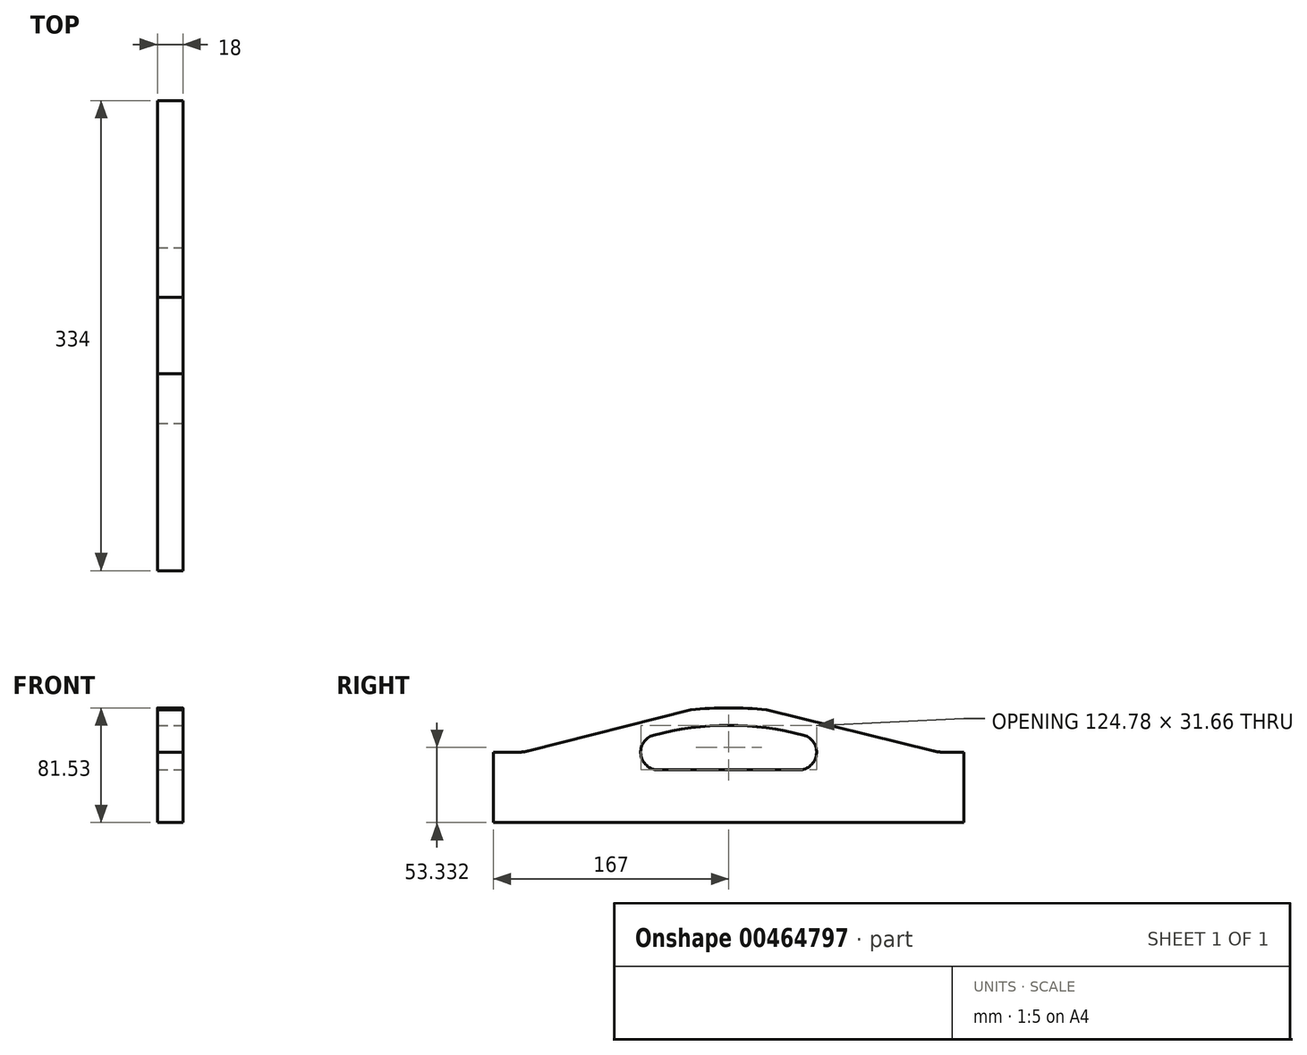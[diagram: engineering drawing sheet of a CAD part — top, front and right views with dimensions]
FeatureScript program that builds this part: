
annotation { "Feature Type Name" : "Feature", "Feature Type Description" : "" }
export const myFeature = defineFeature(function(context is Context, id is Id, definition is map)
    precondition{}
    {
        {
            var Q0;
            Q0=qCreatedBy(makeId("Right.planeOp"),FACE);
            var sketch = newSketch(context, id + "F0", { "sketchPlane" : qUnion([Q0])});
            skLineSegment(sketch, "E0.bottom", {"start": v(0, 0) * mm, "end": v(334, 0) * mm});
            skLineSegment(sketch, "E0.top", {"start": v(0, 100) * mm, "end": v(334, 100) * mm, "construction": true});
            skLineSegment(sketch, "E0.left", {"start": v(0, 0) * mm, "end": v(0, 100) * mm});
            skLineSegment(sketch, "E0.right", {"start": v(334, 0) * mm, "end": v(334, 100) * mm});
            skLineSegment(sketch, "E1", {"start": v(0, 50) * mm, "end": v(17.4, 50) * mm, "construction": true});
            skPoint(sketch, "E2", {"position": v(140, 100) * mm});
            skPoint(sketch, "E3", {"position": v(194, 100) * mm});
            skLineSegment(sketch, "E4", {"start": v(140, 100) * mm, "end": v(140, 0) * mm});
            skLineSegment(sketch, "E5", {"start": v(194, 100) * mm, "end": v(194, 0) * mm});
            skArc(sketch, "E6", {"start": v(140, 80) * mm, "mid": v(167, 81.53) * mm, "end": v(194, 80) * mm});
            skLineSegment(sketch, "E7", {"start": v(0, 50) * mm, "end": v(18, 50) * mm});
            skLineSegment(sketch, "E8", {"start": v(24.73, 50.91) * mm, "end": v(140, 80) * mm});
            skLineSegment(sketch, "E9", {"start": v(334, 50) * mm, "end": v(319.63, 50) * mm});
            skLineSegment(sketch, "E10", {"start": v(312.47, 50.87) * mm, "end": v(194, 80) * mm});
            skPoint(sketch, "E11.newPointB", {"position": v(334, 50) * mm});
            skArc(sketch, "E11.filletArc", {"start": v(17.4, 50) * mm, "mid": v(21.1, 50.23) * mm, "end": v(24.73, 50.91) * mm});
            skPoint(sketch, "E12.visualSharp", {"position": v(316, 50) * mm});
            skArc(sketch, "E12.filletArc", {"start": v(312.47, 50.87) * mm, "mid": v(316.03, 50.22) * mm, "end": v(319.63, 50) * mm});
            skSolve(sketch);
        }
        {
            var Q0;
            Q0=qSketchRegion(id+"F0",true);
            extrude(context, id + "F1", {"entities" : qUnion([Q0]), "depth" : 18 * mm});
        }
        {
            var Q0;
            Q0=makeQuery(id+"F1.opExtrude","CAP_FACE",FACE,{"disambiguationData":[OSD([sQuery(id+"F0.wireOp",EDGE,"E0.bottom"),sQuery(id+"F0.wireOp",EDGE,"E0.left"),sQuery(id+"F0.wireOp",EDGE,"E0.right"),sQuery(id+"F0.wireOp",EDGE,"hojcP1TL-Xpnx-iaRk-RxsB-XFSz29LCahgp"),sQuery(id+"F0.wireOp",EDGE,"atJYV5Rb-Yel0-aSoY-TR2I-Oknle9Pxrf5G"),sQuery(id+"F0.wireOp",EDGE,"E6")])],"isStart":false});
            var sketch = newSketch(context, id + "F2", { "sketchPlane" : qUnion([Q0])});
            skLineSegment(sketch, "E13", {"start": v(117, 62.5) * mm, "end": v(117, 37.5) * mm, "construction": true});
            skLineSegment(sketch, "E14", {"start": v(217, 62.5) * mm, "end": v(217, 37.5) * mm, "construction": true});
            skLineSegment(sketch, "E15", {"start": v(117, 37.5) * mm, "end": v(217, 37.5) * mm});
            skArc(sketch, "E16", {"start": v(104.5, 50) * mm, "mid": v(108.16, 41.16) * mm, "end": v(117, 37.5) * mm});
            skArc(sketch, "E17", {"start": v(217, 37.5) * mm, "mid": v(225.84, 41.16) * mm, "end": v(229.5, 50) * mm});
            skLineSegment(sketch, "E18", {"start": v(167, 50) * mm, "end": v(167, -134.27) * mm, "construction": true});
            skLineSegment(sketch, "E19", {"start": v(167, -134.27) * mm, "end": v(117, 50) * mm, "construction": true});
            skLineSegment(sketch, "E20", {"start": v(167, -134.27) * mm, "end": v(217, 50) * mm, "construction": true});
            skLineSegment(sketch, "E21", {"start": v(117, 50) * mm, "end": v(110.86, 72.65) * mm, "construction": true});
            skLineSegment(sketch, "E22", {"start": v(217, 50) * mm, "end": v(223.2, 72.82) * mm, "construction": true});
            skArc(sketch, "E23", {"start": v(113.73, 62.06) * mm, "mid": v(107.07, 57.6) * mm, "end": v(104.5, 50) * mm});
            skArc(sketch, "E24", {"start": v(229.5, 50) * mm, "mid": v(226.93, 57.6) * mm, "end": v(220.27, 62.06) * mm});
            skArc(sketch, "E25", {"start": v(113.73, 62.06) * mm, "mid": v(167, 69.16) * mm, "end": v(220.27, 62.06) * mm});
            skLineSegment(sketch, "E26", {"start": v(0, 50) * mm, "end": v(334, 50) * mm, "construction": true});
            skSolve(sketch);
        }
        {
            var Q0;
            Q0=qSketchRegion(id+"F2",true);
            extrude(context, id + "F3", {"entities" : qUnion([Q0]), "operationType" : NewBodyOperationType.REMOVE, "oppositeDirection" : true, "depth" : 25 * mm});
        }
    });
